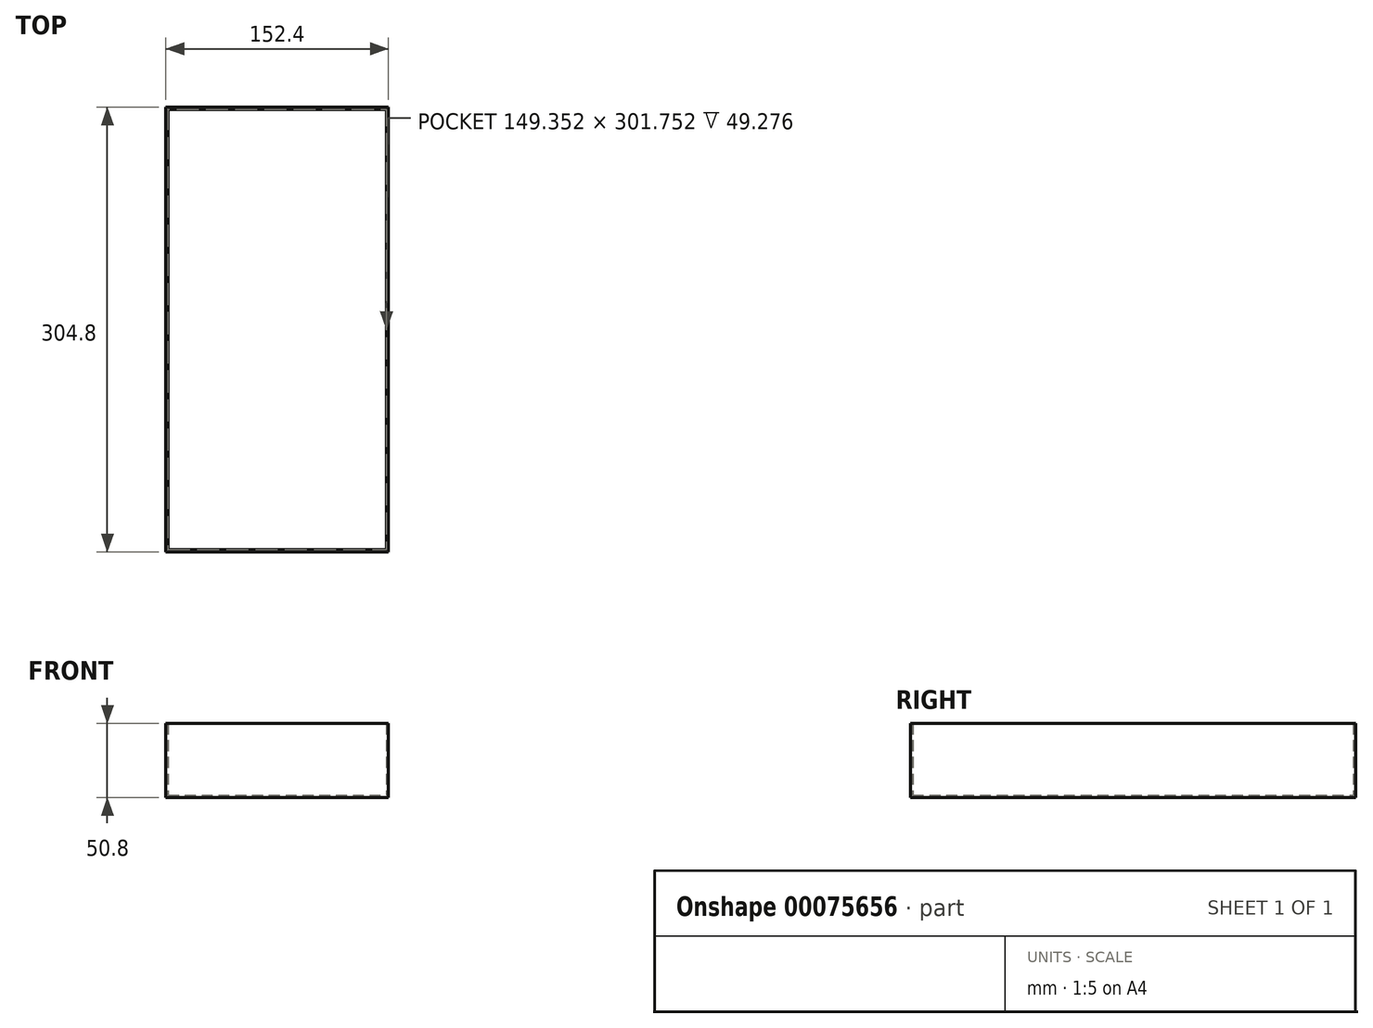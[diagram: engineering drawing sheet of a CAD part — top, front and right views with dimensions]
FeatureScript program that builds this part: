
annotation { "Feature Type Name" : "Feature", "Feature Type Description" : "" }
export const myFeature = defineFeature(function(context is Context, id is Id, definition is map)
    precondition{}
    {
        {
            var Q0;
            Q0=qCreatedBy(makeId("Front.planeOp"),FACE);
            var sketch = newSketch(context, id + "F0", { "sketchPlane" : qUnion([Q0])});
            skLineSegment(sketch, "E0.bottom", {"start": v(-112.9, 33.6) * mm, "end": v(39.5, 33.6) * mm});
            skLineSegment(sketch, "E0.top", {"start": v(-112.9, -17.2) * mm, "end": v(39.5, -17.2) * mm});
            skLineSegment(sketch, "E0.left", {"start": v(-112.9, 33.6) * mm, "end": v(-112.9, -17.2) * mm});
            skLineSegment(sketch, "E0.right", {"start": v(39.5, 33.6) * mm, "end": v(39.5, -17.2) * mm});
            skSolve(sketch);
        }
        {
            var Q0;
            Q0=makeQuery(id+"F0.imprint","IMPRINT",FACE,{"disambiguationData":[TD([[makeQuery(id+"F0.imprint","IMPRINT",EDGE,{"derivedFrom":sQuery(id+"F0.wireOp",EDGE,"E0.bottom")}),-1.0]])]});
            extrude(context, id + "F1", {"entities" : qUnion([Q0]), "endBound" : BoundingType.SYMMETRIC, "depth" : 304.8 * mm});
        }
        {
            var Q0;
            Q0=makeQuery(id+"F1.opExtrude","SWEPT_FACE",FACE,{"disambiguationData":[OSD([sQuery(id+"F0.wireOp",EDGE,"E0.bottom")])]});
            shell(context, id + "F2", {"entities" : qUnion([Q0]), "thickness" : 1.52 * mm});
        }
    });
